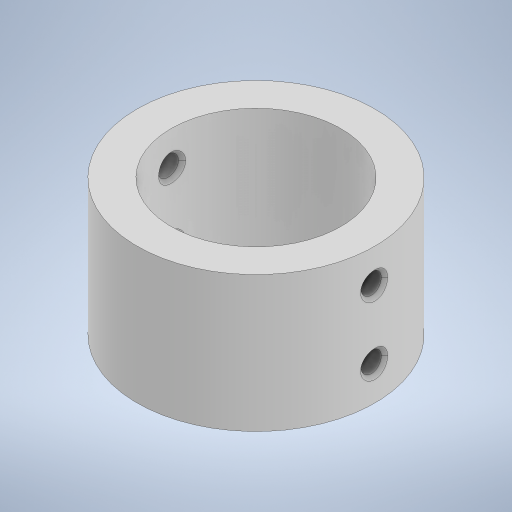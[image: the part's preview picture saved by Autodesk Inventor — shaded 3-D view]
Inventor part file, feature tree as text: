
AUTODESK INVENTOR PART (.ipt)
format: ipt  version: 2023 (Build 270158000, 158)  size: 304,640 bytes
history: native  units: mm
features: extrude x2, sketch x2, other x1, chamfer x1
ambient origin geometry x8: Origin, YZ Plane, XZ Plane, XY Plane, X Axis, Y Axis, Z Axis, Center Point
bodies: Body1 (feature_tree)
feature tree (6):
  other  "Твердое тело1"
  extrude  "Выдавливание1"  Depth=25.0mm
  extrude  "Выдавливание2"  Depth=35.0mm
  chamfer  "Фаска1"  Distance=20.0mm
  sketch  "Эскиз1"
  sketch  "Эскиз2"
